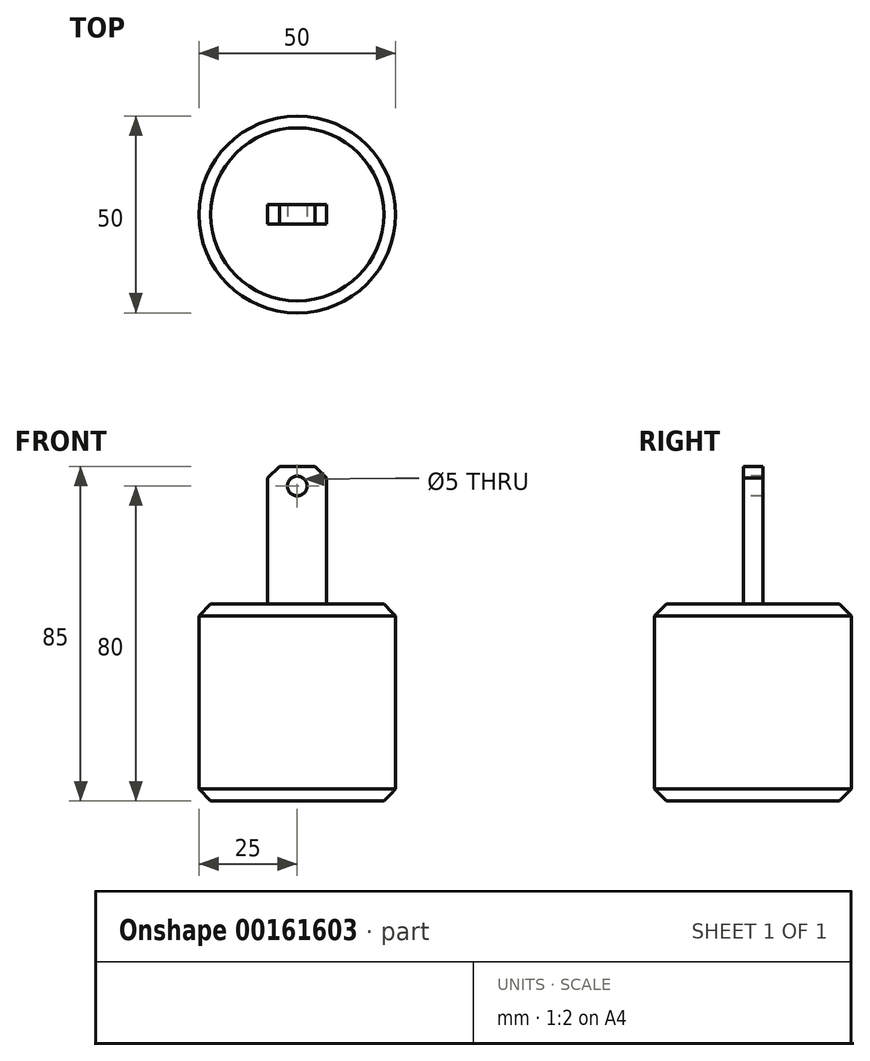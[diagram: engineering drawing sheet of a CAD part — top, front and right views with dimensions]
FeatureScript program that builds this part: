
annotation { "Feature Type Name" : "Feature", "Feature Type Description" : "" }
export const myFeature = defineFeature(function(context is Context, id is Id, definition is map)
    precondition{}
    {
        {
            var Q0;
            Q0=qCreatedBy(makeId("Top.planeOp"),FACE);
            var sketch = newSketch(context, id + "F0", { "sketchPlane" : qUnion([Q0])});
            skCircle(sketch, "E0", {"center": v(0, 0) * mm, "radius": 25 * mm});
            skSolve(sketch);
        }
        {
            var Q0;
            Q0 = qSketchRegion(id + "F0", true);
            extrude(context, id + "F1", {"entities" : qUnion([Q0]), "endBound" : BoundingType.SYMMETRIC, "depth" : 50 * mm});
        }
        {
            var Q0;
            Q0=makeQuery(id+"F1.opExtrude","CAP_FACE",FACE,{"disambiguationData":[OSD([sQuery(id+"F0.wireOp",EDGE,"E0")])],"isStart":false});
            var sketch = newSketch(context, id + "F2", { "sketchPlane" : qUnion([Q0])});
            skLineSegment(sketch, "E1.bottom", {"start": v(-7.5, 2.5) * mm, "end": v(7.5, 2.5) * mm});
            skLineSegment(sketch, "E1.top", {"start": v(-7.5, -2.5) * mm, "end": v(7.5, -2.5) * mm});
            skLineSegment(sketch, "E1.left", {"start": v(-7.5, 2.5) * mm, "end": v(-7.5, -2.5) * mm});
            skLineSegment(sketch, "E1.right", {"start": v(7.5, 2.5) * mm, "end": v(7.5, -2.5) * mm});
            skPoint(sketch, "E1.middle", {"position": v(0, 0) * mm});
            skSolve(sketch);
        }
        {
            var Q0;
            Q0 = qSketchRegion(id + "F2", true);
            extrude(context, id + "F3", {"entities" : qUnion([Q0]), "operationType" : NewBodyOperationType.ADD, "depth" : 35 * mm});
        }
        {
            var Q0;
            Q0=makeQuery(id+"F3.opExtrude","SWEPT_FACE",FACE,{"disambiguationData":[OSD([sQuery(id+"F2.wireOp",EDGE,"E1.top")])]});
            var sketch = newSketch(context, id + "F4", { "sketchPlane" : qUnion([Q0])});
            skCircle(sketch, "E2", {"center": v(0, 55) * mm, "radius": 2.5 * mm});
            skSolve(sketch);
        }
        {
            var Q0;
            Q0 = qSketchRegion(id + "F4", true);
            extrude(context, id + "F5", {"entities" : qUnion([Q0]), "operationType" : NewBodyOperationType.REMOVE, "endBound" : BoundingType.UP_TO_NEXT, "oppositeDirection" : true, "depth" : 25 * mm});
        }
        {
            var Q0;
            Q0=makeQuery(id+"F1.opExtrude","CAP_EDGE",EDGE,{"disambiguationData":[OSD([sQuery(id+"F0.wireOp",EDGE,"E0")])],"isStart":false});
            var Q1;
            Q1=makeQuery(id+"F1.opExtrude","CAP_EDGE",EDGE,{"disambiguationData":[OSD([sQuery(id+"F0.wireOp",EDGE,"E0")])],"isStart":true});
            var Q2;
            Q2=makeQuery(id+"F3.opExtrude","CAP_EDGE",EDGE,{"disambiguationData":[OSD([sQuery(id+"F2.wireOp",EDGE,"E1.left")])],"isStart":false});
            var Q3;
            Q3=makeQuery(id+"F3.opExtrude","CAP_EDGE",EDGE,{"disambiguationData":[OSD([sQuery(id+"F2.wireOp",EDGE,"E1.right")])],"isStart":false});
            chamfer(context, id + "F6", {"entities" : qUnion([Q0, Q1, Q2, Q3]), "width" : 3 * mm, "tangentPropagation" : true});
        }
    });
